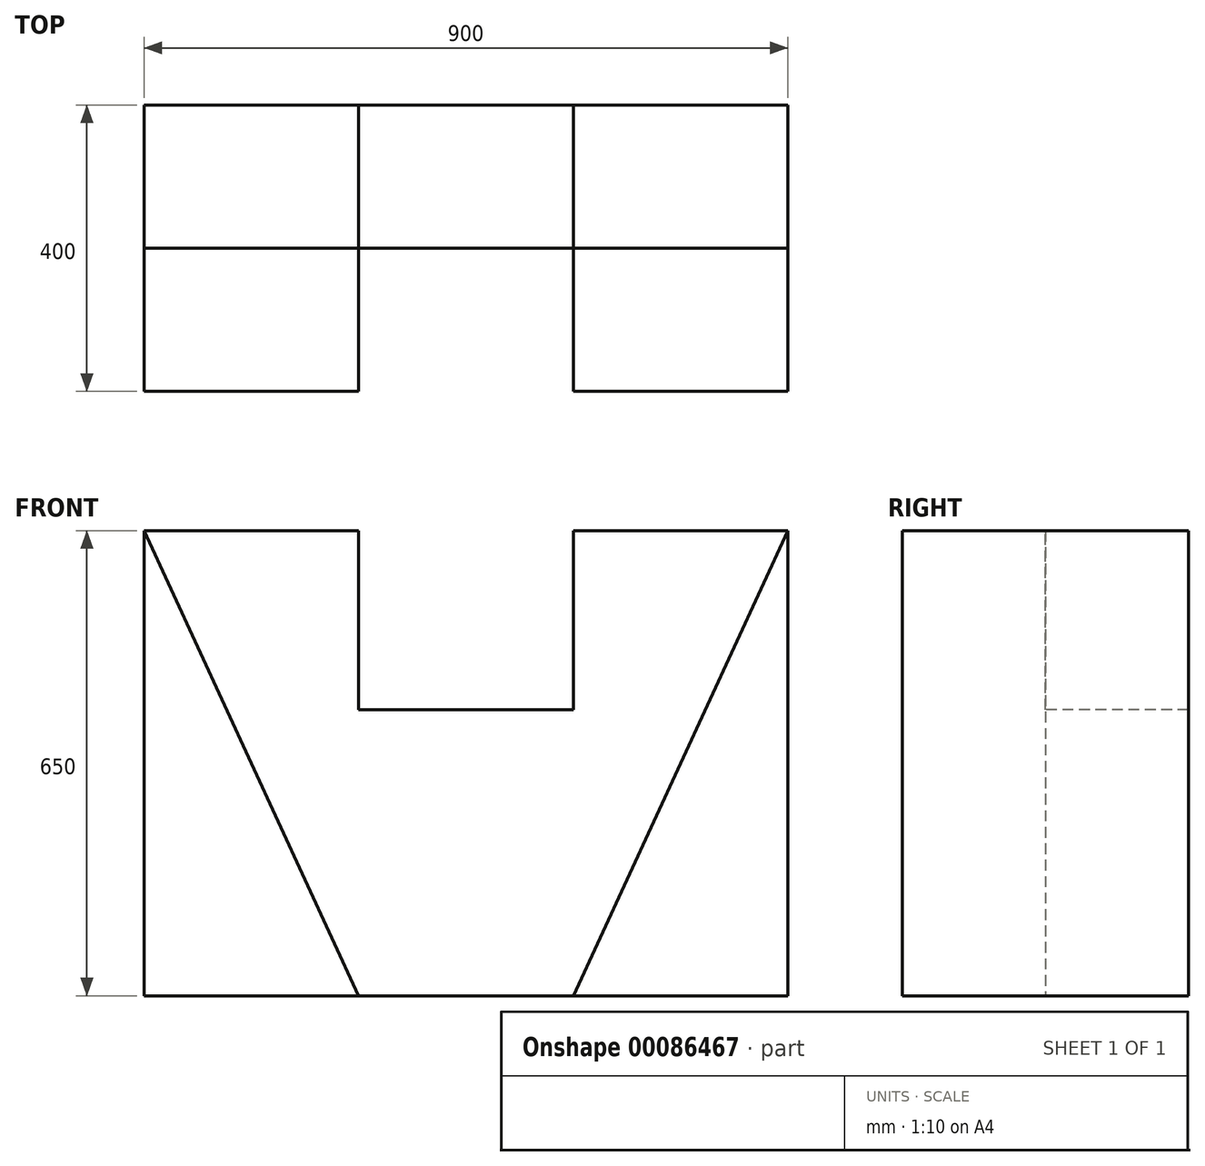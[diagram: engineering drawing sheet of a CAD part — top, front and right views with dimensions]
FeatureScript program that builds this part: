
annotation { "Feature Type Name" : "Feature", "Feature Type Description" : "" }
export const myFeature = defineFeature(function(context is Context, id is Id, definition is map)
    precondition{}
    {
        {
            var Q0;
            Q0=qCreatedBy(makeId("Front.planeOp"),FACE);
            var sketch = newSketch(context, id + "F0", { "sketchPlane" : qUnion([Q0])});
            skLineSegment(sketch, "E0.bottom", {"start": v(450, -325) * mm, "end": v(-450, -325) * mm});
            skLineSegment(sketch, "E0.top", {"start": v(450, 325) * mm, "end": v(-450, 325) * mm});
            skLineSegment(sketch, "E0.left", {"start": v(450, -325) * mm, "end": v(450, 325) * mm});
            skLineSegment(sketch, "E0.right", {"start": v(-450, -325) * mm, "end": v(-450, 325) * mm});
            skPoint(sketch, "E0.middle", {"position": v(0, 0) * mm});
            skSolve(sketch);
        }
        {
            var Q0;
            Q0 = qSketchRegion(id + "F0", true);
            extrude(context, id + "F1", {"entities" : qUnion([Q0]), "depth" : 400 * mm});
        }
        {
            var Q0;
            Q0=makeQuery(id+"F1.opExtrude","CAP_FACE",FACE,{"disambiguationData":[OSD([sQuery(id+"F0.wireOp",EDGE,"E0.bottom"),sQuery(id+"F0.wireOp",EDGE,"E0.top"),sQuery(id+"F0.wireOp",EDGE,"E0.left"),sQuery(id+"F0.wireOp",EDGE,"E0.right")])],"isStart":false});
            var sketch = newSketch(context, id + "F2", { "sketchPlane" : qUnion([Q0])});
            skLineSegment(sketch, "E1", {"start": v(-450, 325) * mm, "end": v(-150, -325) * mm});
            skLineSegment(sketch, "E2", {"start": v(-150, -325) * mm, "end": v(150, -325) * mm});
            skLineSegment(sketch, "E3", {"start": v(150, -325) * mm, "end": v(450, 325) * mm});
            skLineSegment(sketch, "E4", {"start": v(-450, 325) * mm, "end": v(450, 325) * mm});
            skPoint(sketch, "E5", {"position": v(0, -325) * mm});
            skSolve(sketch);
        }
        {
            var Q0;
            Q0 = qSketchRegion(id + "F2", true);
            extrude(context, id + "F3", {"entities" : qUnion([Q0]), "operationType" : NewBodyOperationType.REMOVE, "oppositeDirection" : true, "depth" : 200 * mm});
        }
        {
            var Q0;
            Q0=makeQuery(id+"F3.boolean.opBoolean","COPY",FACE,{"derivedFrom":makeQuery(id+"F3.opExtrude","CAP_FACE",FACE,{"disambiguationData":[OSD([sQuery(id+"F2.wireOp",EDGE,"E1"),sQuery(id+"F2.wireOp",EDGE,"E2"),sQuery(id+"F2.wireOp",EDGE,"E3"),sQuery(id+"F2.wireOp",EDGE,"E4")])],"isStart":false})});
            var sketch = newSketch(context, id + "F4", { "sketchPlane" : qUnion([Q0])});
            skLineSegment(sketch, "E6.bottom", {"start": v(150, 75) * mm, "end": v(-150, 75) * mm});
            skLineSegment(sketch, "E6.top", {"start": v(150, 575) * mm, "end": v(-150, 575) * mm});
            skLineSegment(sketch, "E6.left", {"start": v(150, 75) * mm, "end": v(150, 575) * mm});
            skLineSegment(sketch, "E6.right", {"start": v(-150, 75) * mm, "end": v(-150, 575) * mm});
            skPoint(sketch, "E6.middle", {"position": v(0, 325) * mm});
            skSolve(sketch);
        }
        {
            var Q0;
            {var subQ0=sQuery(id+"F4.wireOp",EDGE,"E6.bottom");Q0=makeQuery(id+"F4.imprint","IMPRINT",FACE,{"disambiguationData":[TD([[makeQuery(id+"F4.imprint","IMPRINT",EDGE,{"derivedFrom":subQ0}),-1.0]])]});}
            var Q1;
            {var subQ0=sQuery(id+"F4.wireOp",EDGE,"E6.top");Q1=makeQuery(id+"F4.imprint","IMPRINT",FACE,{"disambiguationData":[TD([[makeQuery(id+"F4.imprint","IMPRINT",EDGE,{"derivedFrom":subQ0}),1.0]])]});}
            extrude(context, id + "F5", {"entities" : qUnion([Q0, Q1]), "operationType" : NewBodyOperationType.REMOVE, "endBound" : BoundingType.THROUGH_ALL, "oppositeDirection" : true, "depth" : 53 * mm});
        }
    });
